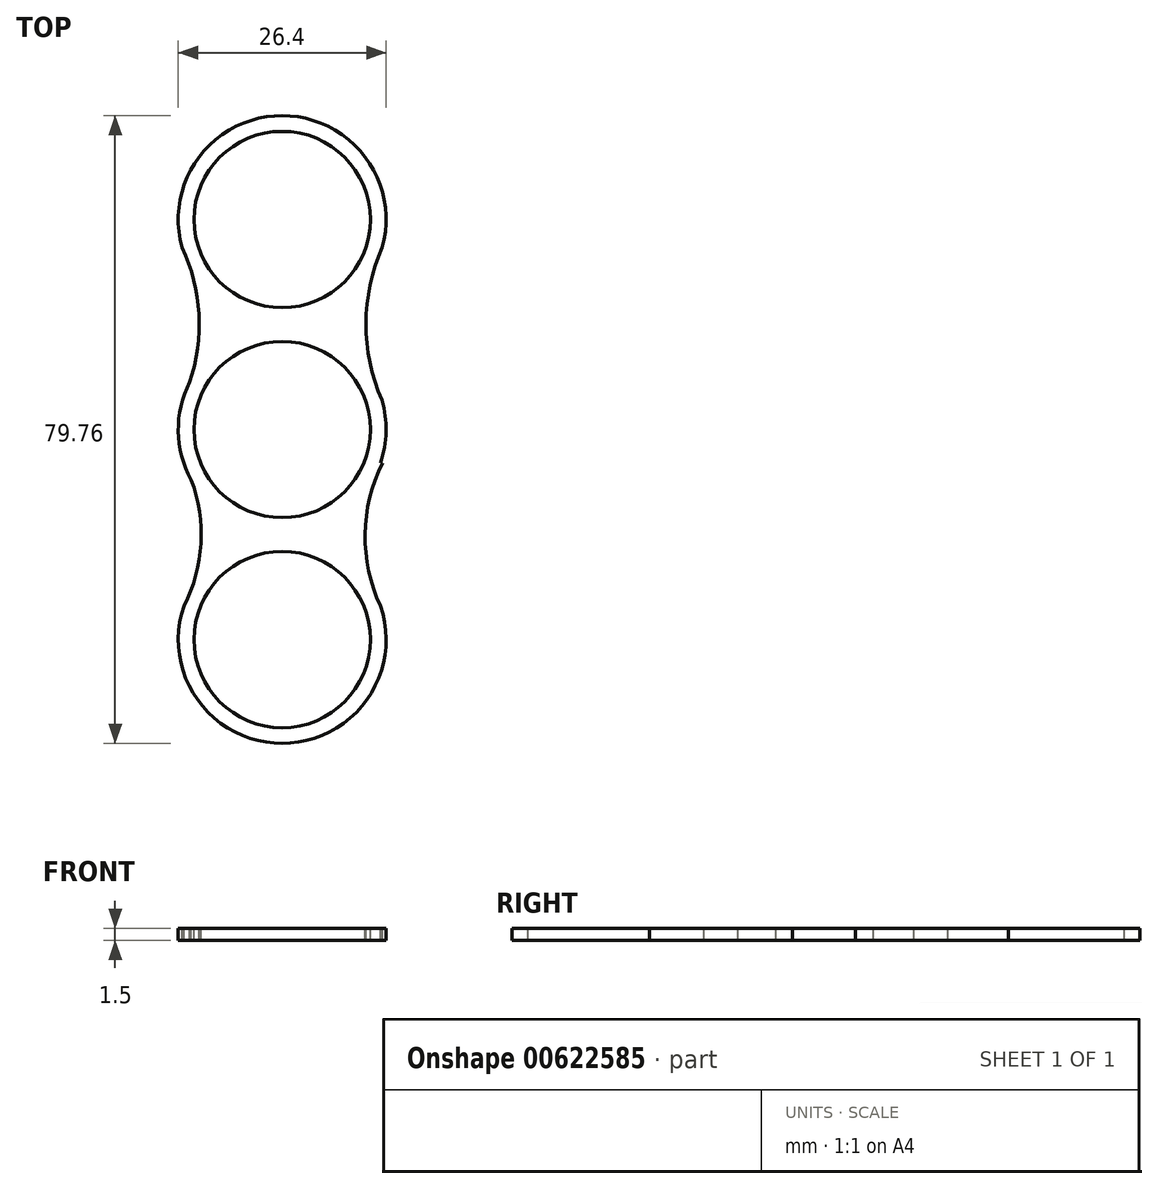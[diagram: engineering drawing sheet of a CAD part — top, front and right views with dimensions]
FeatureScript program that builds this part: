
annotation { "Feature Type Name" : "Feature", "Feature Type Description" : "" }
export const myFeature = defineFeature(function(context is Context, id is Id, definition is map)
    precondition{}
    {
        {
            var Q0;
            Q0=qCreatedBy(makeId("Top.planeOp"),FACE);
            var sketch = newSketch(context, id + "F0", { "sketchPlane" : qUnion([Q0])});
            skCircle(sketch, "E0", {"center": v(0, 0) * mm, "radius": 11.2 * mm});
            skArc(sketch, "E1", {"start": v(-11.75, 6) * mm, "mid": v(-13.2, -0.21) * mm, "end": v(-11.55, -6.39) * mm});
            skCircle(sketch, "E2", {"center": v(0, 26.68) * mm, "radius": 11.2 * mm});
            skArc(sketch, "E3", {"start": v(12.72, 23.14) * mm, "mid": v(0, 39.88) * mm, "end": v(-12.72, 23.14) * mm});
            skArc(sketch, "E4.1.0", {"start": v(-12.5, -22.4) * mm, "mid": v(0, -39.88) * mm, "end": v(12.5, -22.4) * mm});
            skCircle(sketch, "E4.1.1", {"center": v(0, -26.68) * mm, "radius": 11.2 * mm});
            skArc(sketch, "E5", {"start": v(12.74, -4.28) * mm, "mid": v(10.53, -13.32) * mm, "end": v(12.5, -22.4) * mm});
            skArc(sketch, "E6", {"start": v(12.72, 23.14) * mm, "mid": v(10.64, 13.45) * mm, "end": v(12.66, 3.75) * mm});
            skLineSegment(sketch, "E7", {"start": v(12.72, 23.14) * mm, "end": v(10.63, 23.14) * mm, "construction": true});
            skLineSegment(sketch, "E8", {"start": v(12.74, -4.28) * mm, "end": v(12.49, -4.28) * mm, "construction": true});
            skArc(sketch, "E9", {"start": v(-11.75, 6) * mm, "mid": v(-10.57, 14.67) * mm, "end": v(-12.72, 23.14) * mm});
            skArc(sketch, "E10", {"start": v(-12.5, -22.4) * mm, "mid": v(-10.32, -14.5) * mm, "end": v(-11.55, -6.39) * mm});
            skArc(sketch, "E11.trimOffspring", {"start": v(12.49, -4.28) * mm, "mid": v(13.2, -0.28) * mm, "end": v(12.66, 3.75) * mm});
            skSolve(sketch);
        }
        {
            var Q0;
            Q0=sQuery(id+"F0.wireOp",EDGE,"E10");
            var Q1;
            Q1=sQuery(id+"F0.wireOp",EDGE,"E4.1.0");
            var Q2;
            Q2=sQuery(id+"F0.wireOp",EDGE,"E5");
            var Q3;
            Q3=sQuery(id+"F0.wireOp",EDGE,"E11.trimOffspring");
            var Q4;
            Q4=sQuery(id+"F0.wireOp",EDGE,"E6");
            var Q5;
            Q5=sQuery(id+"F0.wireOp",EDGE,"E1");
            var Q6;
            Q6=sQuery(id+"F0.wireOp",EDGE,"E3");
            var Q7;
            Q7=sQuery(id+"F0.wireOp",EDGE,"E9");
            var Q8;
            Q8=sQuery(id+"F0.wireOp",EDGE,"E0");
            var Q9;
            Q9=sQuery(id+"F0.wireOp",EDGE,"E4.1.1");
            var Q10;
            Q10=sQuery(id+"F0.wireOp",EDGE,"E2");
            extrude(context, id + "F1", {"bodyType" : ToolBodyType.SURFACE, "operationType" : NewBodyOperationType.INTERSECT, "surfaceEntities" : qUnion([Q0, Q1, Q2, Q3, Q4, Q5, Q6, Q7, Q8, Q9, Q10]), "depth" : 1.5 * mm, "offsetDistance" : 25 * mm});
        }
    });
